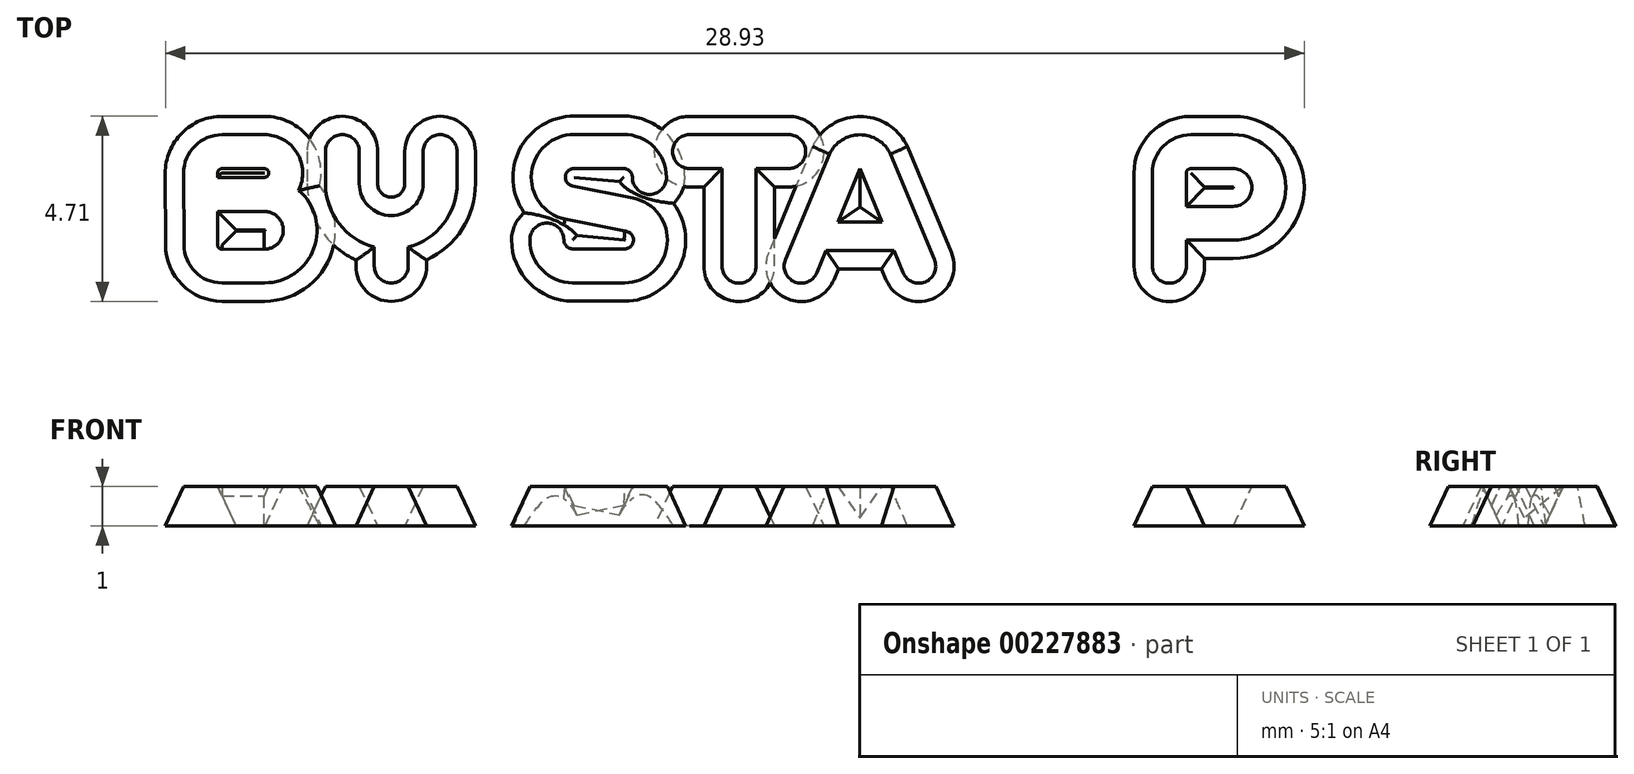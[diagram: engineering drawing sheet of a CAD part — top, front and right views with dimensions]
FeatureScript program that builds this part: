
annotation { "Feature Type Name" : "Feature", "Feature Type Description" : "" }
export const myFeature = defineFeature(function(context is Context, id is Id, definition is map)
    precondition{}
    {
        {
            var Q0;
            Q0=qCreatedBy(makeId("Top.planeOp"),FACE);
            var sketch = newSketch(context, id + "F0", { "sketchPlane" : qUnion([Q0])});
            skArc(sketch, "E0", {"start": v(7.3, -25.16) * mm, "mid": v(6.86, -24.73) * mm, "end": v(6.43, -25.16) * mm});
            skLineSegment(sketch, "E1", {"start": v(6.43, -25.16) * mm, "end": v(7.3, -25.16) * mm, "construction": true});
            skArc(sketch, "E2", {"start": v(9.78, -25.16) * mm, "mid": v(9.35, -24.73) * mm, "end": v(8.92, -25.16) * mm});
            skLineSegment(sketch, "E3", {"start": v(8.92, -25.16) * mm, "end": v(9.78, -25.16) * mm, "construction": true});
            skLineSegment(sketch, "E4", {"start": v(7.3, -25.16) * mm, "end": v(7.3, -25.97) * mm});
            skLineSegment(sketch, "E5", {"start": v(8.92, -25.16) * mm, "end": v(8.92, -25.97) * mm});
            skLineSegment(sketch, "E6", {"start": v(9.78, -25.16) * mm, "end": v(9.78, -25.97) * mm});
            skLineSegment(sketch, "E7", {"start": v(6.43, -25.16) * mm, "end": v(6.43, -25.97) * mm});
            skArc(sketch, "E8", {"start": v(7.3, -25.97) * mm, "mid": v(8.1, -26.79) * mm, "end": v(8.92, -25.97) * mm});
            skArc(sketch, "E9", {"start": v(6.43, -25.97) * mm, "mid": v(6.78, -27) * mm, "end": v(7.68, -27.6) * mm});
            skArc(sketch, "E10", {"start": v(7.68, -28.07) * mm, "mid": v(8.1, -28.5) * mm, "end": v(8.54, -28.07) * mm});
            skLineSegment(sketch, "E11", {"start": v(8.54, -28.07) * mm, "end": v(7.68, -28.07) * mm, "construction": true});
            skLineSegment(sketch, "E12", {"start": v(8.54, -28.07) * mm, "end": v(8.54, -27.6) * mm});
            skLineSegment(sketch, "E13", {"start": v(7.68, -28.07) * mm, "end": v(7.68, -27.6) * mm});
            skArc(sketch, "E14.trimOffspring", {"start": v(8.54, -27.6) * mm, "mid": v(9.43, -27) * mm, "end": v(9.78, -25.97) * mm});
            skArc(sketch, "E15", {"start": v(15.68, -24.73) * mm, "mid": v(15.25, -25.16) * mm, "end": v(15.68, -25.6) * mm});
            skLineSegment(sketch, "E16", {"start": v(15.68, -25.6) * mm, "end": v(15.68, -24.73) * mm, "construction": true});
            skLineSegment(sketch, "E17", {"start": v(15.68, -25.6) * mm, "end": v(16.51, -25.6) * mm});
            skLineSegment(sketch, "E18", {"start": v(15.68, -24.73) * mm, "end": v(18.2, -24.73) * mm});
            skArc(sketch, "E19", {"start": v(16.51, -28.07) * mm, "mid": v(16.94, -28.5) * mm, "end": v(17.37, -28.07) * mm});
            skLineSegment(sketch, "E20", {"start": v(17.37, -28.07) * mm, "end": v(16.51, -28.07) * mm, "construction": true});
            skLineSegment(sketch, "E21", {"start": v(17.37, -28.07) * mm, "end": v(17.37, -25.6) * mm});
            skLineSegment(sketch, "E22", {"start": v(16.51, -28.07) * mm, "end": v(16.51, -25.6) * mm});
            skArc(sketch, "E23", {"start": v(18.2, -25.6) * mm, "mid": v(18.64, -25.16) * mm, "end": v(18.2, -24.73) * mm});
            skLineSegment(sketch, "E24", {"start": v(18.2, -24.73) * mm, "end": v(18.2, -25.6) * mm, "construction": true});
            skLineSegment(sketch, "E25", {"start": v(18.2, -25.6) * mm, "end": v(17.37, -25.6) * mm});
            skArc(sketch, "E26", {"start": v(27.44, -28.07) * mm, "mid": v(27.87, -28.5) * mm, "end": v(28.3, -28.07) * mm});
            skLineSegment(sketch, "E27", {"start": v(28.3, -28.07) * mm, "end": v(27.44, -28.07) * mm, "construction": true});
            skLineSegment(sketch, "E28", {"start": v(27.44, -28.07) * mm, "end": v(27.44, -25.71) * mm});
            skLineSegment(sketch, "E29", {"start": v(28.3, -28.07) * mm, "end": v(28.3, -27.41) * mm});
            skArc(sketch, "E30", {"start": v(28.3, -25.71) * mm, "mid": v(28.34, -25.63) * mm, "end": v(28.42, -25.6) * mm});
            skArc(sketch, "E31", {"start": v(27.44, -25.71) * mm, "mid": v(27.73, -25.02) * mm, "end": v(28.42, -24.73) * mm});
            skArc(sketch, "E32", {"start": v(29.5, -25.6) * mm, "mid": v(29.97, -26.07) * mm, "end": v(29.5, -26.55) * mm});
            skLineSegment(sketch, "E33", {"start": v(28.42, -25.6) * mm, "end": v(29.5, -25.6) * mm});
            skLineSegment(sketch, "E34", {"start": v(29.5, -26.55) * mm, "end": v(28.3, -26.55) * mm});
            skLineSegment(sketch, "E35", {"start": v(28.3, -26.55) * mm, "end": v(28.3, -25.71) * mm});
            skLineSegment(sketch, "E36", {"start": v(28.42, -24.73) * mm, "end": v(29.5, -24.73) * mm});
            skLineSegment(sketch, "E37", {"start": v(28.3, -27.41) * mm, "end": v(29.5, -27.41) * mm});
            skArc(sketch, "E38", {"start": v(29.5, -24.73) * mm, "mid": v(30.83, -26.07) * mm, "end": v(29.5, -27.41) * mm});
            skLineSegment(sketch, "E39", {"start": v(21.11, -28.24) * mm, "end": v(20.88, -27.67) * mm});
            skArc(sketch, "E40", {"start": v(19.24, -25.22) * mm, "mid": v(20.01, -24.74) * mm, "end": v(20.8, -25.22) * mm});
            skLineSegment(sketch, "E41", {"start": v(20.8, -25.22) * mm, "end": v(21.9, -27.9) * mm});
            skArc(sketch, "E42", {"start": v(21.11, -28.24) * mm, "mid": v(21.68, -28.47) * mm, "end": v(21.9, -27.9) * mm});
            skLineSegment(sketch, "E43", {"start": v(19.46, -26.95) * mm, "end": v(20.57, -26.95) * mm});
            skLineSegment(sketch, "E44.trimOffspring", {"start": v(20.57, -26.95) * mm, "end": v(20.01, -25.6) * mm});
            skLineSegment(sketch, "E45", {"start": v(20.88, -27.67) * mm, "end": v(19.15, -27.67) * mm});
            skLineSegment(sketch, "E46", {"start": v(20.01, -25.6) * mm, "end": v(20.01, -26.52) * mm, "construction": true});
            skLineSegment(sketch, "E47.MirrorCS", {"start": v(19.24, -25.22) * mm, "end": v(18.12, -27.9) * mm});
            skArc(sketch, "E48.MirrorCS", {"start": v(18.92, -28.24) * mm, "mid": v(18.35, -28.47) * mm, "end": v(18.12, -27.9) * mm});
            skLineSegment(sketch, "E49.MirrorCS", {"start": v(19.46, -26.95) * mm, "end": v(20.01, -25.6) * mm});
            skLineSegment(sketch, "E50.MirrorCS", {"start": v(18.92, -28.24) * mm, "end": v(19.15, -27.67) * mm});
            skLineSegment(sketch, "E51", {"start": v(18.52, -28.5) * mm, "end": v(21.5, -28.5) * mm, "construction": true});
            skLineSegment(sketch, "E52", {"start": v(21.11, -28.24) * mm, "end": v(21.9, -27.9) * mm, "construction": true});
            skLineSegment(sketch, "E53", {"start": v(3.7, -26.68) * mm, "end": v(3.7, -27.53) * mm});
            skArc(sketch, "E54", {"start": v(3.7, -27.53) * mm, "mid": v(3.73, -27.61) * mm, "end": v(3.8, -27.64) * mm});
            skLineSegment(sketch, "E55", {"start": v(3.7, -26.68) * mm, "end": v(4.88, -26.68) * mm});
            skLineSegment(sketch, "E56", {"start": v(4.88, -27.64) * mm, "end": v(3.8, -27.64) * mm});
            skArc(sketch, "E57", {"start": v(4.88, -27.64) * mm, "mid": v(5.36, -27.17) * mm, "end": v(4.88, -26.68) * mm});
            skArc(sketch, "E58", {"start": v(2.84, -27.53) * mm, "mid": v(3.12, -28.22) * mm, "end": v(3.8, -28.5) * mm});
            skArc(sketch, "E59", {"start": v(5.75, -26.15) * mm, "mid": v(6.14, -27.62) * mm, "end": v(4.88, -28.5) * mm});
            skLineSegment(sketch, "E60", {"start": v(3.8, -28.5) * mm, "end": v(4.88, -28.5) * mm});
            skArc(sketch, "E61", {"start": v(3.81, -25.6) * mm, "mid": v(3.73, -25.63) * mm, "end": v(3.7, -25.71) * mm});
            skLineSegment(sketch, "E62", {"start": v(3.7, -25.71) * mm, "end": v(3.7, -25.82) * mm});
            skLineSegment(sketch, "E63", {"start": v(3.7, -25.82) * mm, "end": v(4.88, -25.82) * mm});
            skLineSegment(sketch, "E64", {"start": v(3.81, -25.6) * mm, "end": v(4.88, -25.6) * mm});
            skArc(sketch, "E65", {"start": v(4.88, -25.82) * mm, "mid": v(5, -25.7) * mm, "end": v(4.88, -25.6) * mm});
            skArc(sketch, "E66", {"start": v(4.88, -24.73) * mm, "mid": v(5.71, -25.2) * mm, "end": v(5.75, -26.15) * mm});
            skArc(sketch, "E67", {"start": v(3.81, -24.73) * mm, "mid": v(3.12, -25.02) * mm, "end": v(2.83, -25.71) * mm});
            skLineSegment(sketch, "E68", {"start": v(2.83, -25.71) * mm, "end": v(2.84, -27.53) * mm});
            skLineSegment(sketch, "E69", {"start": v(3.81, -24.73) * mm, "end": v(4.88, -24.73) * mm});
            skArc(sketch, "E70", {"start": v(12.5, -27.4) * mm, "mid": v(12.56, -27.57) * mm, "end": v(12.72, -27.63) * mm});
            skArc(sketch, "E71", {"start": v(12.72, -28.5) * mm, "mid": v(11.95, -28.18) * mm, "end": v(11.63, -27.4) * mm});
            skArc(sketch, "E72", {"start": v(11.63, -27.4) * mm, "mid": v(12.06, -26.98) * mm, "end": v(12.5, -27.4) * mm});
            skArc(sketch, "E73", {"start": v(14.04, -27.63) * mm, "mid": v(14.26, -27.41) * mm, "end": v(14.04, -27.18) * mm});
            skLineSegment(sketch, "E74", {"start": v(12.72, -27.63) * mm, "end": v(14.04, -27.63) * mm});
            skLineSegment(sketch, "E75", {"start": v(12.72, -28.5) * mm, "end": v(14.04, -28.5) * mm});
            skArc(sketch, "E76", {"start": v(14.04, -28.5) * mm, "mid": v(15.12, -27.52) * mm, "end": v(14.25, -26.34) * mm});
            skLineSegment(sketch, "E77", {"start": v(12.52, -26.88) * mm, "end": v(14.04, -27.18) * mm});
            skArc(sketch, "E78", {"start": v(14, -24.72) * mm, "mid": v(14.78, -25.04) * mm, "end": v(15.1, -25.82) * mm});
            skArc(sketch, "E79", {"start": v(14, -25.6) * mm, "mid": v(14.17, -25.66) * mm, "end": v(14.23, -25.82) * mm});
            skArc(sketch, "E80", {"start": v(14.23, -25.82) * mm, "mid": v(14.67, -26.25) * mm, "end": v(15.1, -25.82) * mm});
            skArc(sketch, "E81", {"start": v(12.75, -25.6) * mm, "mid": v(12.53, -25.8) * mm, "end": v(12.7, -26.04) * mm});
            skLineSegment(sketch, "E82", {"start": v(12.7, -26.04) * mm, "end": v(14.25, -26.34) * mm});
            skLineSegment(sketch, "E83", {"start": v(12.75, -25.82) * mm, "end": v(12.75, -25.6) * mm, "construction": true});
            skLineSegment(sketch, "E84", {"start": v(14.04, -27.4) * mm, "end": v(14.04, -27.63) * mm, "construction": true});
            skLineSegment(sketch, "E85", {"start": v(12.75, -25.6) * mm, "end": v(14, -25.6) * mm});
            skArc(sketch, "E86", {"start": v(12.75, -24.72) * mm, "mid": v(11.67, -25.7) * mm, "end": v(12.52, -26.88) * mm});
            skLineSegment(sketch, "E87", {"start": v(12.75, -24.72) * mm, "end": v(14, -24.72) * mm});
            skArc(sketch, "E88", {"start": v(22.77, -25.27) * mm, "mid": v(23.29, -24.75) * mm, "end": v(23.91, -25.13) * mm});
            skArc(sketch, "E89", {"start": v(22.38, -28.1) * mm, "mid": v(22.77, -28.51) * mm, "end": v(23.22, -28.16) * mm});
            skLineSegment(sketch, "E90", {"start": v(22.77, -25.27) * mm, "end": v(22.38, -28.1) * mm});
            skLineSegment(sketch, "E91", {"start": v(23.22, -28.16) * mm, "end": v(23.47, -26.34) * mm});
            skArc(sketch, "E92", {"start": v(24.13, -28.12) * mm, "mid": v(24.7, -28.51) * mm, "end": v(25.25, -28.1) * mm});
            skLineSegment(sketch, "E93", {"start": v(24.13, -28.12) * mm, "end": v(23.47, -26.34) * mm});
            skLineSegment(sketch, "E94", {"start": v(23.91, -25.13) * mm, "end": v(24.7, -27.21) * mm});
            skArc(sketch, "E95.MirrorCS", {"start": v(27, -28.1) * mm, "mid": v(26.62, -28.51) * mm, "end": v(26.17, -28.16) * mm});
            skLineSegment(sketch, "E96.MirrorCS", {"start": v(26.62, -25.27) * mm, "end": v(27, -28.1) * mm});
            skLineSegment(sketch, "E97.MirrorCS", {"start": v(25.47, -25.13) * mm, "end": v(24.7, -27.21) * mm});
            skArc(sketch, "E98.MirrorCS", {"start": v(26.62, -25.27) * mm, "mid": v(26.1, -24.75) * mm, "end": v(25.47, -25.13) * mm});
            skLineSegment(sketch, "E99.MirrorCS", {"start": v(26.17, -28.16) * mm, "end": v(25.92, -26.34) * mm});
            skLineSegment(sketch, "E100.MirrorCS", {"start": v(25.25, -28.1) * mm, "end": v(25.92, -26.34) * mm});
            skLineSegment(sketch, "E101", {"start": v(2.84, -26.62) * mm, "end": v(16.84, -26.62) * mm, "construction": true});
            skSolve(sketch);
        }
        {
            var Q0;
            Q0=makeQuery(id+"F0.imprint","IMPRINT",FACE,{"disambiguationData":[TD([[makeQuery(id+"F0.imprint","IMPRINT",EDGE,{"derivedFrom":sQuery(id+"F0.wireOp",EDGE,"E53")}),-1.0]])]});
            var Q1;
            Q1=makeQuery(id+"F0.imprint","IMPRINT",FACE,{"disambiguationData":[TD([[makeQuery(id+"F0.imprint","IMPRINT",EDGE,{"derivedFrom":sQuery(id+"F0.wireOp",EDGE,"E0")}),1.0]])]});
            var Q2;
            Q2=makeQuery(id+"F0.imprint","IMPRINT",FACE,{"disambiguationData":[TD([[makeQuery(id+"F0.imprint","IMPRINT",EDGE,{"derivedFrom":sQuery(id+"F0.wireOp",EDGE,"E70")}),-1.0]])]});
            var Q3;
            Q3=makeQuery(id+"F0.imprint","IMPRINT",FACE,{"disambiguationData":[TD([[makeQuery(id+"F0.imprint","IMPRINT",EDGE,{"derivedFrom":sQuery(id+"F0.wireOp",EDGE,"E15")}),1.0]])]});
            var Q4;
            Q4=makeQuery(id+"F0.imprint","IMPRINT",FACE,{"disambiguationData":[TD([[makeQuery(id+"F0.imprint","IMPRINT",EDGE,{"derivedFrom":sQuery(id+"F0.wireOp",EDGE,"E39")}),-1.0]])]});
            var Q5;
            Q5=makeQuery(id+"F0.imprint","IMPRINT",FACE,{"disambiguationData":[TD([[makeQuery(id+"F0.imprint","IMPRINT",EDGE,{"derivedFrom":sQuery(id+"F0.wireOp",EDGE,"E26")}),1.0]])]});
            var Q6;
            Q6=makeQuery(id+"F0.imprint","IMPRINT",FACE,{"disambiguationData":[TD([[makeQuery(id+"F0.imprint","IMPRINT",EDGE,{"derivedFrom":sQuery(id+"F0.wireOp",EDGE,"E88")}),-1.0]])]});
            extrude(context, id + "F1", {"entities" : qUnion([Q0, Q1, Q2, Q3, Q4, Q5, Q6]), "oppositeDirection" : true, "depth" : 1 * mm, "hasDraft" : true, "draftAngle" : 25 * degree, "offsetDistance" : 25 * mm});
        }
    });
